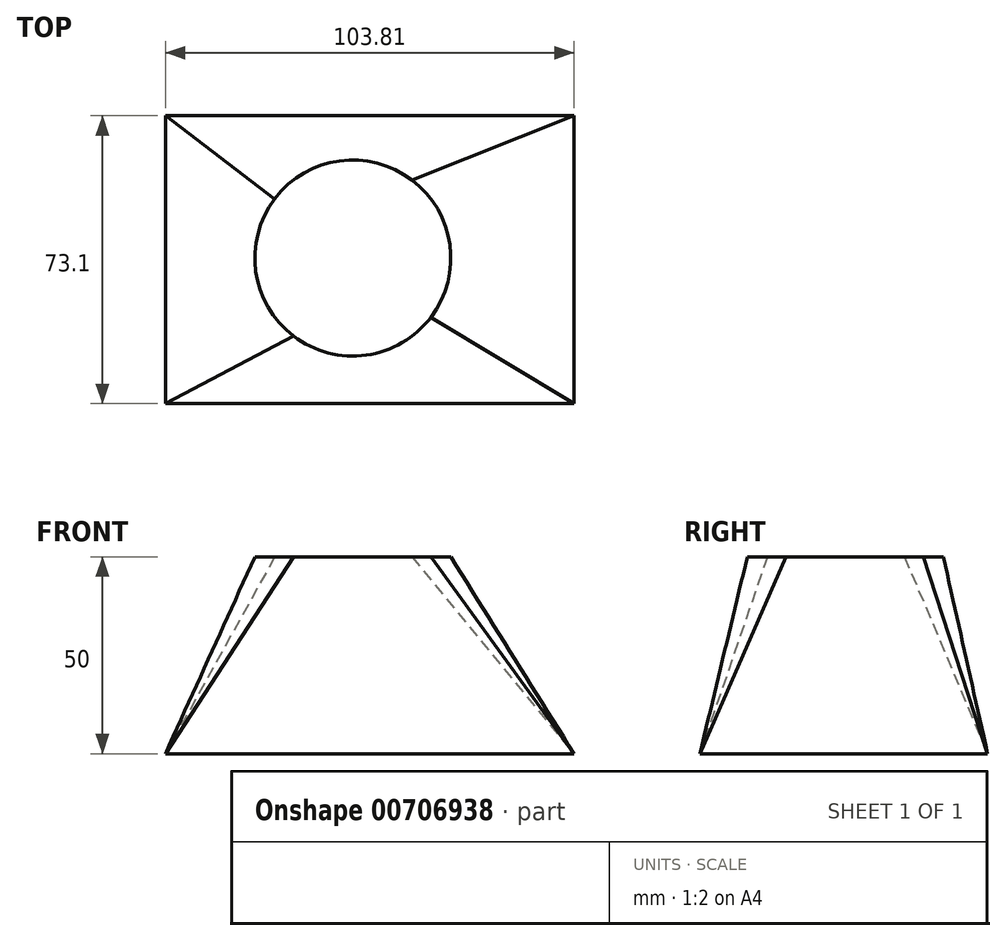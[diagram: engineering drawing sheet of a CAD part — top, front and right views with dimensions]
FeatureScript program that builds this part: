
annotation { "Feature Type Name" : "Feature", "Feature Type Description" : "" }
export const myFeature = defineFeature(function(context is Context, id is Id, definition is map)
    precondition{}
    {
        {
            var Q0;
            Q0=qCreatedBy(makeId("Top.planeOp"),FACE);
            var sketch = newSketch(context, id + "F0", { "sketchPlane" : qUnion([Q0])});
            skLineSegment(sketch, "E0.bottom", {"start": v(-47.63, 36.16) * mm, "end": v(56.18, 36.16) * mm});
            skLineSegment(sketch, "E0.top", {"start": v(-47.63, -36.94) * mm, "end": v(56.18, -36.94) * mm});
            skLineSegment(sketch, "E0.left", {"start": v(-47.63, 36.16) * mm, "end": v(-47.63, -36.94) * mm});
            skLineSegment(sketch, "E0.right", {"start": v(56.18, 36.16) * mm, "end": v(56.18, -36.94) * mm});
            skSolve(sketch);
        }
        {
            var Q0;
            Q0=qCreatedBy(makeId("Top.planeOp"),FACE);
            cPlane(context, id + "F1", {"entities" : qUnion([Q0]), "cplaneType" : CPlaneType.OFFSET, "offset" : 50 * mm, "width" : 150 * mm, "height" : 150 * mm});
        }
        {
            var Q0;
            Q0=qCreatedBy(id+"F1.planeOp",FACE);
            var sketch = newSketch(context, id + "F2", { "sketchPlane" : qUnion([Q0])});
            skCircle(sketch, "E1", {"center": v(0, 0) * mm, "radius": 24.9 * mm});
            skSolve(sketch);
        }
        {
            var Q0;
            Q0=makeQuery(id+"F2.imprint","IMPRINT",FACE,{"disambiguationData":[TD([[makeQuery(id+"F2.imprint","IMPRINT",EDGE,{"derivedFrom":sQuery(id+"F2.wireOp",EDGE,"E1")}),1.0]])]});
            var Q1;
            Q1=makeQuery(id+"F0.imprint","IMPRINT",FACE,{"disambiguationData":[TD([[makeQuery(id+"F0.imprint","IMPRINT",EDGE,{"derivedFrom":sQuery(id+"F0.wireOp",EDGE,"E0.bottom")}),-1.0]])]});
            loft(context, id + "F3", {"sheetProfilesArray" : [{ "sheetProfileEntities" : qUnion([Q0]) }, { "sheetProfileEntities" : qUnion([Q1]) }]});
        }
    });
